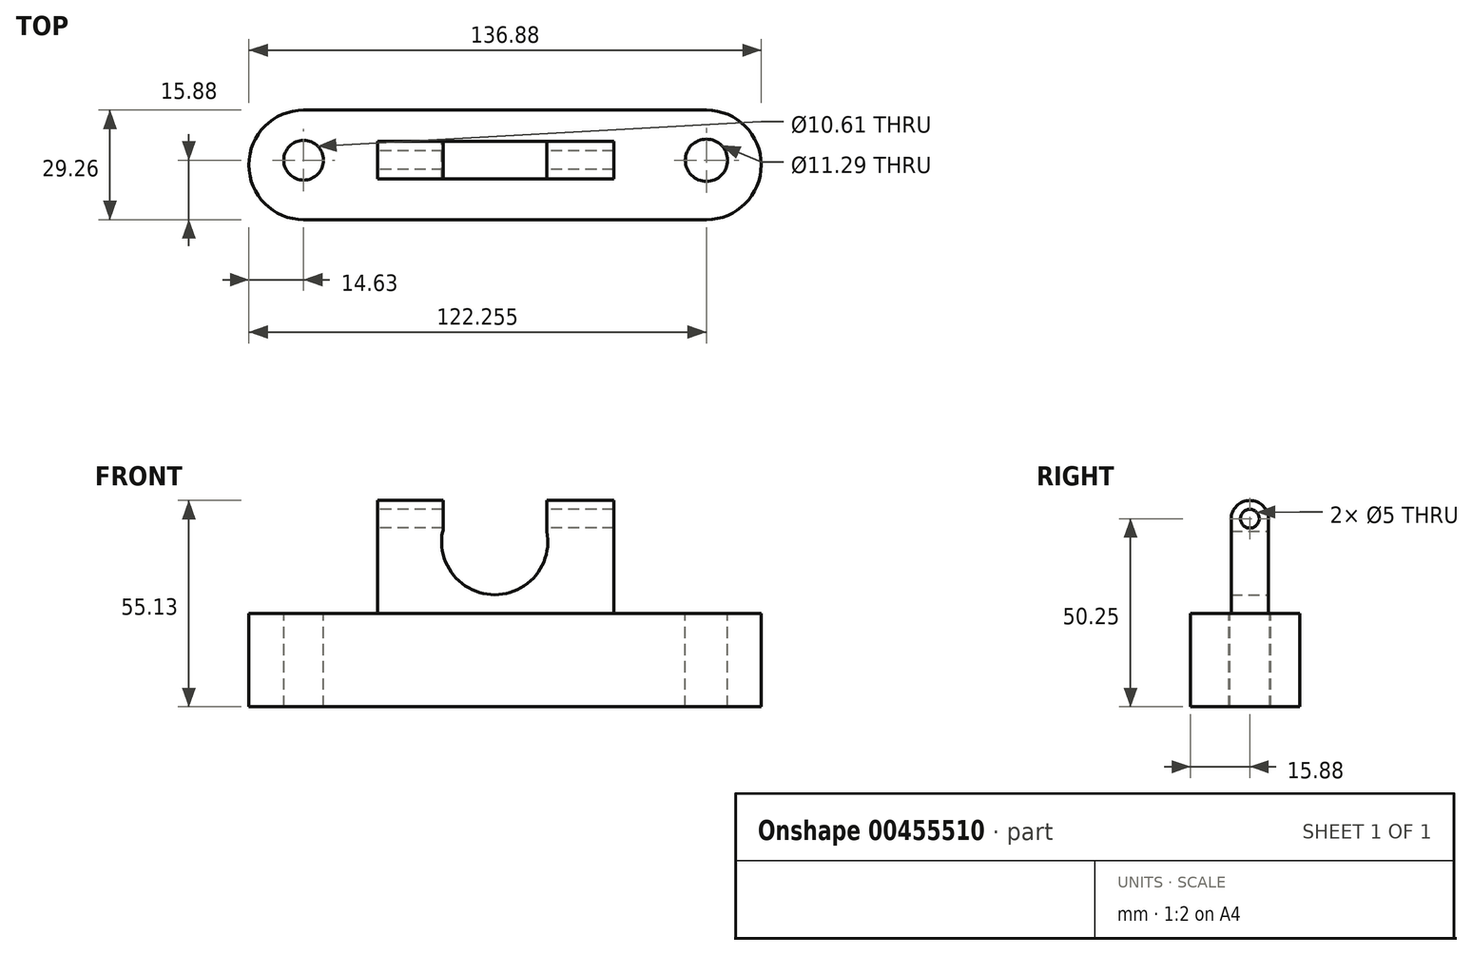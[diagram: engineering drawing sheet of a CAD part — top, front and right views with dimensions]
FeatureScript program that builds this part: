
annotation { "Feature Type Name" : "Feature", "Feature Type Description" : "" }
export const myFeature = defineFeature(function(context is Context, id is Id, definition is map)
    precondition{}
    {
        {
            var Q0;
            Q0=qCreatedBy(makeId("Top.planeOp"),FACE);
            var sketch = newSketch(context, id + "F0", { "sketchPlane" : qUnion([Q0])});
            skLineSegment(sketch, "E0.bottom", {"start": v(-52.25, 13.38) * mm, "end": v(55.38, 13.38) * mm});
            skLineSegment(sketch, "E0.top", {"start": v(-52.25, -15.88) * mm, "end": v(55.38, -15.88) * mm});
            skCircle(sketch, "E1", {"center": v(-52.25, 0) * mm, "radius": 5.3 * mm});
            skArc(sketch, "E2", {"start": v(-52.25, 13.38) * mm, "mid": v(-66.88, -1.25) * mm, "end": v(-52.25, -15.88) * mm});
            skArc(sketch, "E3", {"start": v(55.38, -15.88) * mm, "mid": v(70, -1.25) * mm, "end": v(55.38, 13.38) * mm});
            skCircle(sketch, "E4", {"center": v(55.38, 0) * mm, "radius": 5.65 * mm});
            skSolve(sketch);
        }
        {
            var Q0;
            Q0=qCreatedBy(makeId("Front.planeOp"),FACE);
            var sketch = newSketch(context, id + "F1", { "sketchPlane" : qUnion([Q0])});
            skLineSegment(sketch, "E5.bottom", {"start": v(-32.5, 0) * mm, "end": v(30.63, 0) * mm});
            skLineSegment(sketch, "E5.left", {"start": v(-32.5, 0) * mm, "end": v(-32.5, 21.88) * mm});
            skLineSegment(sketch, "E5.right", {"start": v(30.63, 0) * mm, "end": v(30.63, 21.88) * mm});
            skArc(sketch, "E6", {"start": v(-15.13, 21.88) * mm, "mid": v(-1.19, 4.95) * mm, "end": v(12.75, 21.88) * mm});
            skLineSegment(sketch, "E7.bottom", {"start": v(-15.13, 21.88) * mm, "end": v(-15, 21.88) * mm});
            skLineSegment(sketch, "E7.top", {"start": v(-32.5, 30.13) * mm, "end": v(-15, 30.13) * mm});
            skLineSegment(sketch, "E7.left", {"start": v(-32.5, 21.88) * mm, "end": v(-32.5, 30.13) * mm});
            skLineSegment(sketch, "E7.right", {"start": v(-15, 21.88) * mm, "end": v(-15, 30.13) * mm});
            skLineSegment(sketch, "E8.top", {"start": v(12.75, 30.13) * mm, "end": v(30.63, 30.13) * mm});
            skLineSegment(sketch, "E8.left", {"start": v(12.75, 21.88) * mm, "end": v(12.75, 30.13) * mm});
            skLineSegment(sketch, "E8.right", {"start": v(30.63, 21.88) * mm, "end": v(30.63, 30.13) * mm});
            skSolve(sketch);
        }
        {
            var Q0;
            Q0=makeQuery(id+"F0.imprint","IMPRINT",FACE,{"disambiguationData":[TD([[makeQuery(id+"F0.imprint","IMPRINT",EDGE,{"derivedFrom":sQuery(id+"F0.wireOp",EDGE,"E0.bottom")}),-1.0]])]});
            extrude(context, id + "F2", {"entities" : qUnion([Q0]), "oppositeDirection" : true, "depth" : 25 * mm});
        }
        {
            var Q0;
            Q0=makeQuery(id+"F1.imprint","IMPRINT",FACE,{"disambiguationData":[TD([[makeQuery(id+"F1.imprint","IMPRINT",EDGE,{"derivedFrom":sQuery(id+"F1.wireOp",EDGE,"E5.bottom")}),1.0]])]});
            extrude(context, id + "F3", {"entities" : qUnion([Q0]), "operationType" : NewBodyOperationType.ADD, "depth" : 5 * mm, "hasSecondDirection" : true, "secondDirectionOppositeDirection" : true, "secondDirectionDepth" : 5 * mm});
        }
        {
            var Q0;
            Q0=makeQuery(id+"F3.opExtrude","SWEPT_FACE",FACE,{"disambiguationData":[OSD([sQuery(id+"F1.wireOp",EDGE,"E5.left"),sQuery(id+"F1.wireOp",EDGE,"E7.left")])]});
            var sketch = newSketch(context, id + "F4", { "sketchPlane" : qUnion([Q0])});
            skCircle(sketch, "E9", {"center": v(0, 25.25) * mm, "radius": 2.58 * mm});
            skSolve(sketch);
        }
        {
            var Q0;
            Q0=sQuery(id+"F4.wireOp",VERTEX,"E9.center");
            var Q1;
            Q1=makeQuery(id+"F2.opExtrude","SWEPT_BODY",BODY,{"disambiguationData":[OSD([sQuery(id+"F0.wireOp",EDGE,"E0.bottom"),sQuery(id+"F0.wireOp",EDGE,"E0.top"),sQuery(id+"F0.wireOp",EDGE,"E1"),sQuery(id+"F0.wireOp",EDGE,"E2"),sQuery(id+"F0.wireOp",EDGE,"E3"),sQuery(id+"F0.wireOp",EDGE,"E4")])]});
            hole(context, id + "F5", {"style" : HoleStyle.SIMPLE, "endStyle" : HoleEndStyle.THROUGH, "holeDiameter" : 5 * mm, "isTappedThrough" : true, "tappedDepth" : 12 * mm, "tapClearance" : 3, "locations" : qUnion([Q0]), "scope" : qUnion([Q1])});
        }
        {
            var Q0;
            Q0=makeQuery(id+"F3.opExtrude","CAP_EDGE",EDGE,{"disambiguationData":[OSD([sQuery(id+"F1.wireOp",EDGE,"E8.top")])],"isStart":true});
            var Q1;
            Q1=makeQuery(id+"F3.opExtrude","CAP_EDGE",EDGE,{"disambiguationData":[OSD([sQuery(id+"F1.wireOp",EDGE,"E8.top")])],"isStart":false});
            var Q2;
            Q2=makeQuery(id+"F3.opExtrude","CAP_EDGE",EDGE,{"disambiguationData":[OSD([sQuery(id+"F1.wireOp",EDGE,"E7.top")])],"isStart":true});
            var Q3;
            Q3=makeQuery(id+"F3.opExtrude","CAP_EDGE",EDGE,{"disambiguationData":[OSD([sQuery(id+"F1.wireOp",EDGE,"E7.top")])],"isStart":false});
            fillet(context, id + "F6", {"entities" : qUnion([Q0, Q1, Q2, Q3]), "radius" : 5 * mm, "tangentPropagation" : true, "allowEdgeOverflow" : false});
        }
    });
